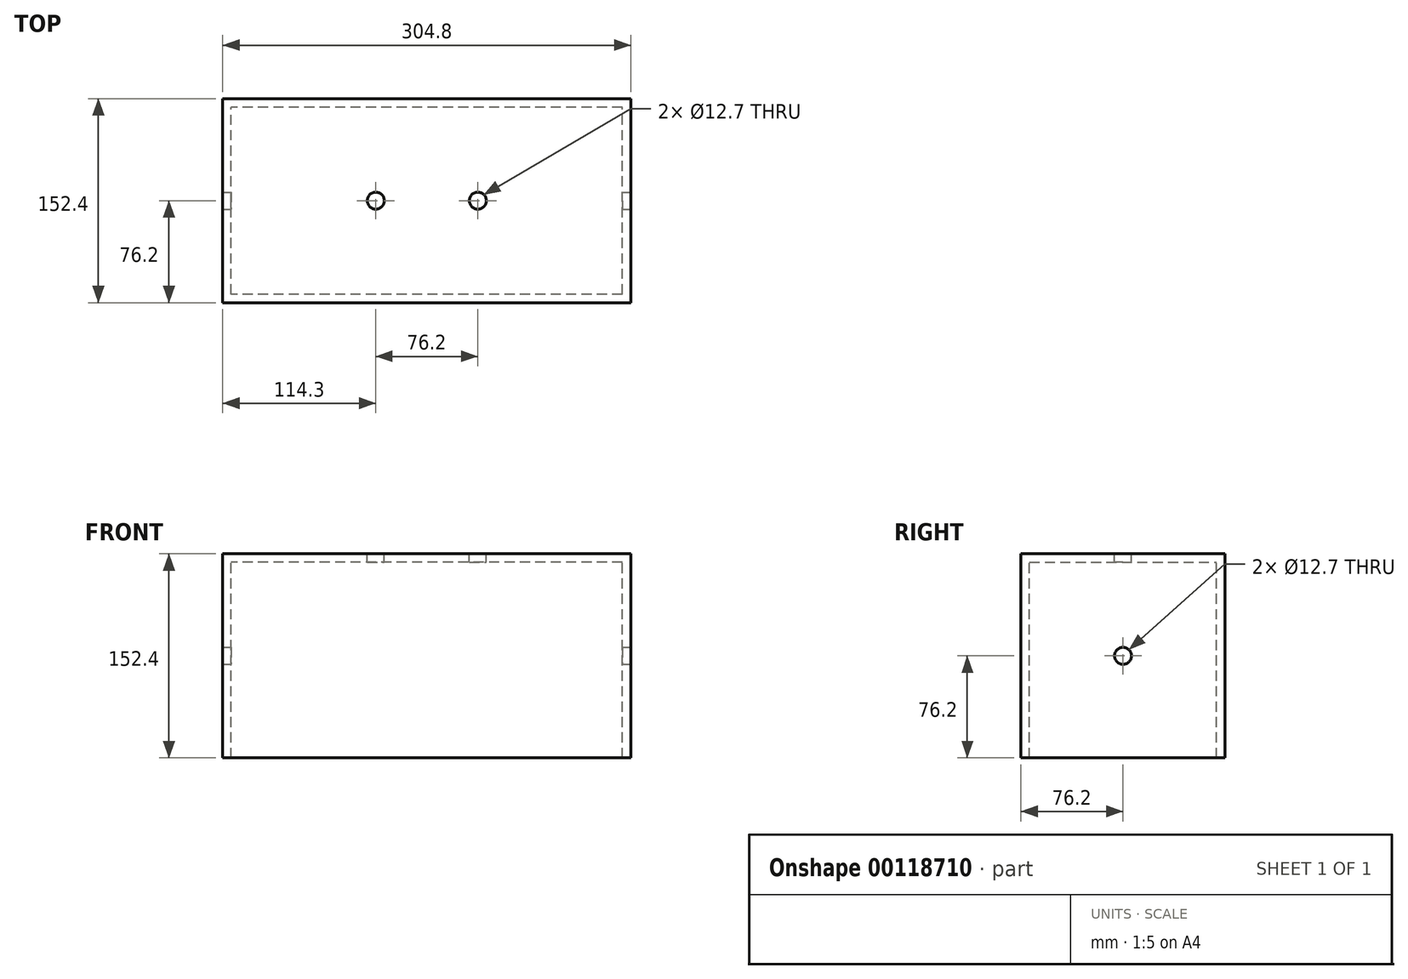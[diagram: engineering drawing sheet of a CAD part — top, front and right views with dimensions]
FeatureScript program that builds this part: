
annotation { "Feature Type Name" : "Feature", "Feature Type Description" : "" }
export const myFeature = defineFeature(function(context is Context, id is Id, definition is map)
    precondition{}
    {
        {
            var Q0;
            Q0=qCreatedBy(makeId("Front.planeOp"),FACE);
            var sketch = newSketch(context, id + "F0", { "sketchPlane" : qUnion([Q0])});
            skLineSegment(sketch, "E0.bottom", {"start": v(152.4, -76.2) * mm, "end": v(-152.4, -76.2) * mm});
            skLineSegment(sketch, "E0.top", {"start": v(152.4, 76.2) * mm, "end": v(-152.4, 76.2) * mm});
            skLineSegment(sketch, "E0.left", {"start": v(152.4, -76.2) * mm, "end": v(152.4, 76.2) * mm});
            skLineSegment(sketch, "E0.right", {"start": v(-152.4, -76.2) * mm, "end": v(-152.4, 76.2) * mm});
            skPoint(sketch, "E0.middle", {"position": v(0, 0) * mm});
            skSolve(sketch);
        }
        {
            var Q0;
            Q0 = qSketchRegion(id + "F0", true);
            extrude(context, id + "F1", {"entities" : qUnion([Q0]), "endBound" : BoundingType.SYMMETRIC, "depth" : 152.4 * mm});
        }
        {
            var Q0;
            Q0=makeQuery(id+"F1.opExtrude","SWEPT_FACE",FACE,{"disambiguationData":[OSD([sQuery(id+"F0.wireOp",EDGE,"E0.bottom")])]});
            shell(context, id + "F2", {"entities" : qUnion([Q0]), "thickness" : 6.35 * mm});
        }
        {
            var Q0;
            Q0=makeQuery(id+"F1.opExtrude","SWEPT_FACE",FACE,{"disambiguationData":[OSD([sQuery(id+"F0.wireOp",EDGE,"E0.left")])]});
            var sketch = newSketch(context, id + "F3", { "sketchPlane" : qUnion([Q0])});
            skCircle(sketch, "E1", {"center": v(0, 0) * mm, "radius": 6.35 * mm});
            skSolve(sketch);
        }
        {
            var Q0;
            Q0 = qSketchRegion(id + "F3", true);
            extrude(context, id + "F4", {"entities" : qUnion([Q0]), "operationType" : NewBodyOperationType.REMOVE, "oppositeDirection" : true, "depth" : 434.16 * mm});
        }
        {
            var Q0;
            Q0=makeQuery(id+"F1.opExtrude","SWEPT_FACE",FACE,{"disambiguationData":[OSD([sQuery(id+"F0.wireOp",EDGE,"E0.top")])]});
            var sketch = newSketch(context, id + "F5", { "sketchPlane" : qUnion([Q0])});
            skCircle(sketch, "E2", {"center": v(-38.1, 0) * mm, "radius": 6.35 * mm});
            skCircle(sketch, "E3", {"center": v(38.1, 0) * mm, "radius": 6.35 * mm});
            skSolve(sketch);
        }
        {
            var Q0;
            Q0 = qSketchRegion(id + "F5", true);
            extrude(context, id + "F6", {"entities" : qUnion([Q0]), "operationType" : NewBodyOperationType.REMOVE, "oppositeDirection" : true, "depth" : 64.02 * mm});
        }
    });
